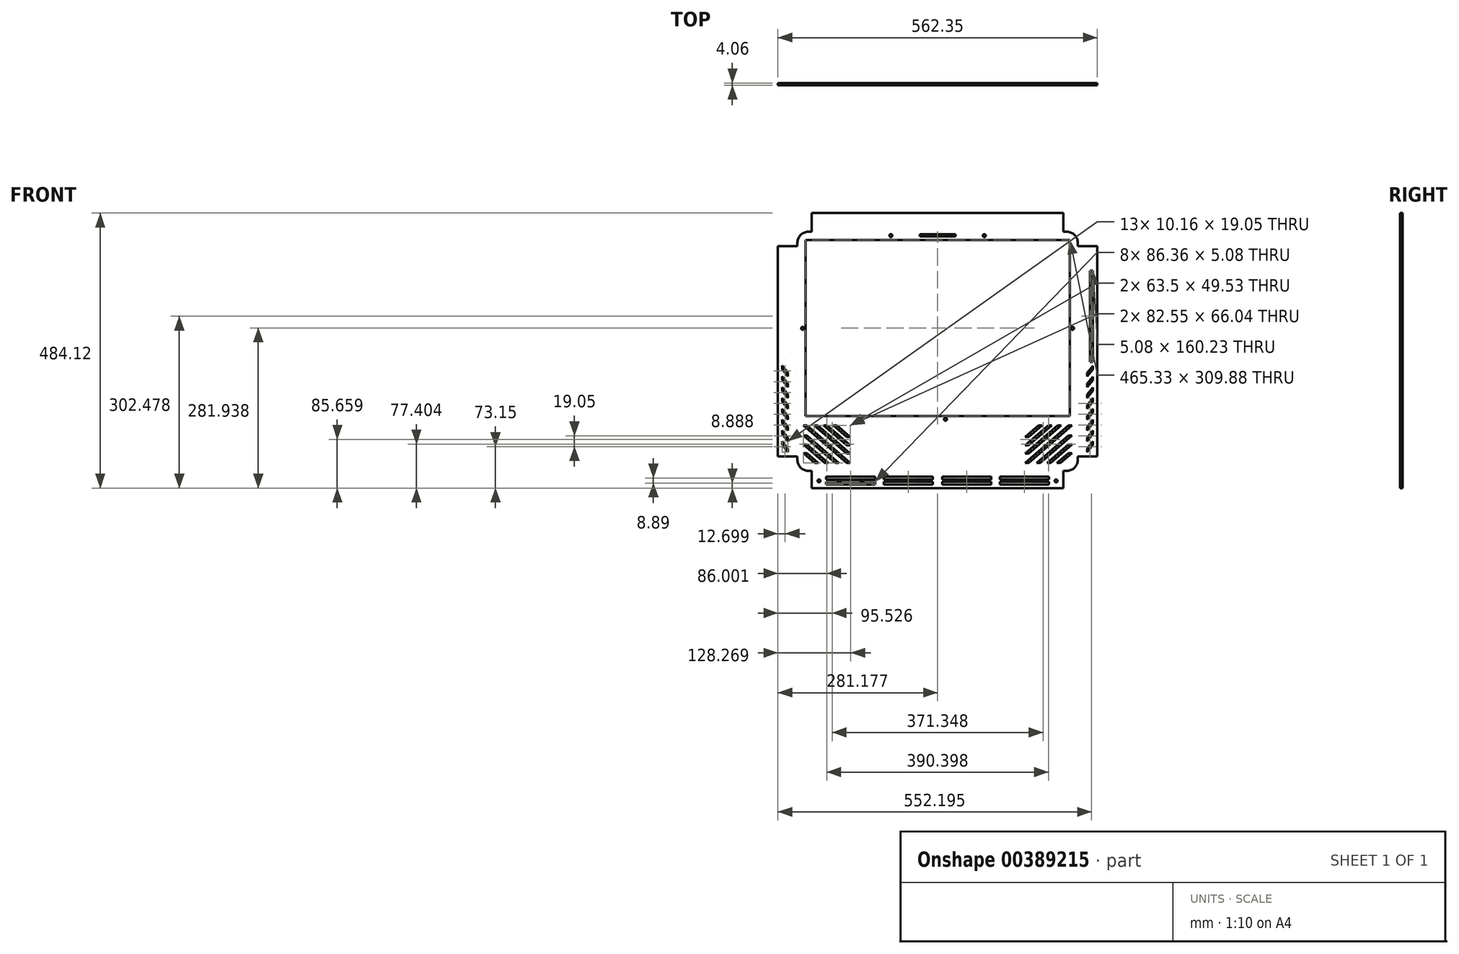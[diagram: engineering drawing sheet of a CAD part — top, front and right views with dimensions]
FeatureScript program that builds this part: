
annotation { "Feature Type Name" : "Feature", "Feature Type Description" : "" }
export const myFeature = defineFeature(function(context is Context, id is Id, definition is map)
    precondition{}
    {
        {
            var Q0;
            Q0=qCreatedBy(makeId("Front.planeOp"),FACE);
            var sketch = newSketch(context, id + "F0", { "sketchPlane" : qUnion([Q0])});
            skLineSegment(sketch, "E0.bottom", {"start": v(112.47, 222.87) * mm, "end": v(-343.2, 222.87) * mm});
            skLineSegment(sketch, "E0.top", {"start": v(112.47, -197.75) * mm, "end": v(-343.2, -197.75) * mm});
            skLineSegment(sketch, "E0.left", {"start": v(131.52, 203.82) * mm, "end": v(131.52, -178.7) * mm});
            skLineSegment(sketch, "E0.right", {"start": v(-362.25, 203.82) * mm, "end": v(-362.25, -178.7) * mm});
            skPoint(sketch, "E0.middle", {"position": v(-115.36, 12.56) * mm});
            skPoint(sketch, "E1.visualSharp", {"position": v(-362.25, 222.87) * mm});
            skArc(sketch, "E1.filletArc", {"start": v(-343.2, 222.87) * mm, "mid": v(-356.67, 217.3) * mm, "end": v(-362.25, 203.82) * mm});
            skPoint(sketch, "E2.visualSharp", {"position": v(131.52, 222.87) * mm});
            skArc(sketch, "E2.filletArc", {"start": v(131.52, 203.82) * mm, "mid": v(125.95, 217.3) * mm, "end": v(112.47, 222.87) * mm});
            skPoint(sketch, "E3.visualSharp", {"position": v(131.52, -197.75) * mm});
            skArc(sketch, "E3.filletArc", {"start": v(112.47, -197.75) * mm, "mid": v(125.95, -192.17) * mm, "end": v(131.52, -178.7) * mm});
            skPoint(sketch, "E4.visualSharp", {"position": v(-362.25, -197.75) * mm});
            skArc(sketch, "E4.filletArc", {"start": v(-362.25, -178.7) * mm, "mid": v(-356.67, -192.17) * mm, "end": v(-343.2, -197.75) * mm});
            skPoint(sketch, "E5.visualSharp", {"position": v(177.9, 212.68) * mm});
            skLineSegment(sketch, "E6.bottom", {"start": v(108.41, 218.8) * mm, "end": v(-339.14, 218.8) * mm});
            skLineSegment(sketch, "E6.left", {"start": v(127.46, 199.76) * mm, "end": v(127.46, -93.36) * mm});
            skLineSegment(sketch, "E6.right", {"start": v(-358.19, 199.76) * mm, "end": v(-358.19, -93.36) * mm});
            skPoint(sketch, "E7.visualSharp", {"position": v(127.46, 218.8) * mm});
            skArc(sketch, "E7.filletArc", {"start": v(127.46, 199.76) * mm, "mid": v(121.88, 213.23) * mm, "end": v(108.41, 218.8) * mm});
            skPoint(sketch, "E8.visualSharp", {"position": v(-358.19, 218.8) * mm});
            skArc(sketch, "E8.filletArc", {"start": v(-339.14, 218.8) * mm, "mid": v(-352.6, 213.23) * mm, "end": v(-358.19, 199.76) * mm});
            skPoint(sketch, "E9.visualSharp", {"position": v(-358.19, -112.4) * mm});
            skPoint(sketch, "E10.visualSharp", {"position": v(127.46, -112.4) * mm});
            skLineSegment(sketch, "E11.bottom", {"start": v(131.52, 197.47) * mm, "end": v(165.81, 197.47) * mm});
            skLineSegment(sketch, "E11.top", {"start": v(131.52, -172.35) * mm, "end": v(165.81, -172.35) * mm});
            skLineSegment(sketch, "E11.left", {"start": v(131.52, 197.47) * mm, "end": v(131.52, -172.35) * mm});
            skLineSegment(sketch, "E11.right", {"start": v(165.81, 197.47) * mm, "end": v(165.81, -172.35) * mm});
            skLineSegment(sketch, "E12.bottom", {"start": v(-396.54, 197.47) * mm, "end": v(-362.25, 197.47) * mm});
            skLineSegment(sketch, "E12.top", {"start": v(-396.54, -172.35) * mm, "end": v(-362.25, -172.35) * mm});
            skLineSegment(sketch, "E12.left", {"start": v(-396.54, 197.47) * mm, "end": v(-396.54, -172.35) * mm});
            skLineSegment(sketch, "E12.right", {"start": v(-362.25, 197.47) * mm, "end": v(-362.25, -172.35) * mm});
            skLineSegment(sketch, "E13.bottom", {"start": v(-336.85, 255.9) * mm, "end": v(106.12, 255.9) * mm});
            skLineSegment(sketch, "E13.top", {"start": v(-336.85, 222.87) * mm, "end": v(106.12, 222.87) * mm});
            skLineSegment(sketch, "E13.left", {"start": v(-336.85, 255.9) * mm, "end": v(-336.85, 222.87) * mm});
            skLineSegment(sketch, "E13.right", {"start": v(106.12, 255.9) * mm, "end": v(106.12, 222.87) * mm});
            skLineSegment(sketch, "E14.bottom", {"start": v(-336.85, -197.75) * mm, "end": v(106.12, -197.75) * mm});
            skLineSegment(sketch, "E14.top", {"start": v(-336.85, -228.23) * mm, "end": v(106.12, -228.23) * mm});
            skLineSegment(sketch, "E14.left", {"start": v(-336.85, -197.75) * mm, "end": v(-336.85, -228.23) * mm});
            skLineSegment(sketch, "E14.right", {"start": v(106.12, -197.75) * mm, "end": v(106.12, -228.23) * mm});
            skSolve(sketch);
        }
        {
            var Q0;
            Q0 = qSketchRegion(id + "F0", true);
            extrude(context, id + "F1", {"entities" : qUnion([Q0]), "depth" : 4.06 * mm});
        }
        {
            var Q0;
            Q0=qCreatedBy(makeId("Front.planeOp"),FACE);
            var sketch = newSketch(context, id + "F2", { "sketchPlane" : qUnion([Q0])});
            skPoint(sketch, "E15.visualSharp", {"position": v(-358.19, 218.8) * mm});
            skPoint(sketch, "E16.visualSharp", {"position": v(127.46, 218.8) * mm});
            skPoint(sketch, "E17.visualSharp", {"position": v(-358.19, -111.4) * mm});
            skPoint(sketch, "E18.visualSharp", {"position": v(127.46, -111.4) * mm});
            skLineSegment(sketch, "E19.bottom", {"start": v(-348.03, 208.65) * mm, "end": v(117.3, 208.65) * mm});
            skLineSegment(sketch, "E19.top", {"start": v(-348.03, -101.23) * mm, "end": v(117.3, -101.23) * mm});
            skLineSegment(sketch, "E19.left", {"start": v(-348.03, 208.65) * mm, "end": v(-348.03, -101.23) * mm});
            skLineSegment(sketch, "E19.right", {"start": v(117.3, 208.65) * mm, "end": v(117.3, -101.23) * mm});
            skSolve(sketch);
        }
        {
            var Q0;
            Q0 = qSketchRegion(id + "F2", true);
            extrude(context, id + "F3", {"entities" : qUnion([Q0]), "operationType" : NewBodyOperationType.REMOVE, "depth" : 4.06 * mm});
        }
        {
            var Q0;
            Q0=qCreatedBy(makeId("Front.planeOp"),FACE);
            var sketch = newSketch(context, id + "F4", { "sketchPlane" : qUnion([Q0])});
            skCircle(sketch, "E20", {"center": v(-101.4, -106.97) * mm, "radius": 2.54 * mm});
            skCircle(sketch, "E21", {"center": v(122.38, 53.05) * mm, "radius": 2.54 * mm});
            skCircle(sketch, "E22", {"center": v(-353.1, 53.05) * mm, "radius": 2.54 * mm});
            skCircle(sketch, "E23", {"center": v(-197.66, 216.27) * mm, "radius": 2.54 * mm});
            skCircle(sketch, "E24", {"center": v(-33.07, 216.27) * mm, "radius": 2.54 * mm});
            skLineSegment(sketch, "E25.bottom", {"start": v(-146.86, 218.8) * mm, "end": v(-83.87, 218.8) * mm});
            skLineSegment(sketch, "E25.top", {"start": v(-146.86, 215) * mm, "end": v(-83.87, 215) * mm});
            skLineSegment(sketch, "E25.left", {"start": v(-146.86, 218.8) * mm, "end": v(-146.86, 215) * mm});
            skLineSegment(sketch, "E25.right", {"start": v(-83.87, 218.8) * mm, "end": v(-83.87, 215) * mm});
            skSolve(sketch);
        }
        {
            var Q0;
            Q0 = qSketchRegion(id + "F4", true);
            extrude(context, id + "F5", {"entities" : qUnion([Q0]), "operationType" : NewBodyOperationType.REMOVE, "depth" : 25.4 * mm});
        }
        {
            var Q0;
            Q0=qCreatedBy(makeId("Front.planeOp"),FACE);
            var sketch = newSketch(context, id + "F6", { "sketchPlane" : qUnion([Q0])});
            skLineSegment(sketch, "E26", {"start": v(-351.81, -117.8) * mm, "end": v(-345.46, -117.8) * mm});
            skLineSegment(sketch, "E27", {"start": v(-345.46, -117.8) * mm, "end": v(-269.26, -183.85) * mm});
            skLineSegment(sketch, "E28", {"start": v(-269.26, -183.85) * mm, "end": v(-275.61, -183.85) * mm});
            skLineSegment(sketch, "E29", {"start": v(-275.61, -183.85) * mm, "end": v(-351.81, -117.8) * mm});
            skLineSegment(sketch, "E30", {"start": v(-332.76, -117.8) * mm, "end": v(-326.41, -117.8) * mm});
            skPoint(sketch, "E31.endSnap0", {"position": v(-272.44, -183.85) * mm});
            skLineSegment(sketch, "E32", {"start": v(-269.26, -167.34) * mm, "end": v(-275.61, -167.34) * mm});
            skLineSegment(sketch, "E33", {"start": v(-275.61, -167.34) * mm, "end": v(-332.76, -117.8) * mm});
            skLineSegment(sketch, "E34", {"start": v(-326.41, -117.8) * mm, "end": v(-269.26, -167.34) * mm});
            skLineSegment(sketch, "E35", {"start": v(-351.81, -135.42) * mm, "end": v(-345.46, -135.42) * mm});
            skLineSegment(sketch, "E36", {"start": v(-345.46, -135.42) * mm, "end": v(-289.6, -183.85) * mm});
            skLineSegment(sketch, "E37", {"start": v(-289.6, -183.85) * mm, "end": v(-295.94, -183.85) * mm});
            skLineSegment(sketch, "E38", {"start": v(-295.94, -183.85) * mm, "end": v(-351.81, -135.42) * mm});
            skLineSegment(sketch, "E39", {"start": v(-351.81, -151.37) * mm, "end": v(-345.46, -151.37) * mm});
            skLineSegment(sketch, "E40", {"start": v(-345.46, -151.37) * mm, "end": v(-307.99, -183.85) * mm});
            skLineSegment(sketch, "E41", {"start": v(-307.99, -183.85) * mm, "end": v(-314.34, -183.85) * mm});
            skLineSegment(sketch, "E42", {"start": v(-314.34, -183.85) * mm, "end": v(-351.81, -151.37) * mm});
            skLineSegment(sketch, "E43", {"start": v(-351.81, -166.54) * mm, "end": v(-345.46, -166.54) * mm});
            skLineSegment(sketch, "E44", {"start": v(-345.46, -166.54) * mm, "end": v(-325.5, -183.85) * mm});
            skLineSegment(sketch, "E45", {"start": v(-325.5, -183.85) * mm, "end": v(-331.85, -183.85) * mm});
            skLineSegment(sketch, "E46", {"start": v(-331.85, -183.85) * mm, "end": v(-351.81, -166.54) * mm});
            skLineSegment(sketch, "E47", {"start": v(-269.26, -153.13) * mm, "end": v(-275.61, -153.13) * mm});
            skLineSegment(sketch, "E48", {"start": v(-275.61, -153.13) * mm, "end": v(-316.37, -117.8) * mm});
            skLineSegment(sketch, "E49", {"start": v(-316.37, -117.8) * mm, "end": v(-310.02, -117.8) * mm});
            skLineSegment(sketch, "E50", {"start": v(-310.02, -117.8) * mm, "end": v(-269.26, -153.13) * mm});
            skLineSegment(sketch, "E51", {"start": v(-269.26, -138.28) * mm, "end": v(-275.61, -138.28) * mm});
            skLineSegment(sketch, "E52", {"start": v(-275.61, -138.28) * mm, "end": v(-299.24, -117.8) * mm});
            skLineSegment(sketch, "E53", {"start": v(-299.24, -117.8) * mm, "end": v(-292.89, -117.8) * mm});
            skLineSegment(sketch, "E54", {"start": v(-292.89, -117.8) * mm, "end": v(-269.26, -138.28) * mm});
            skLineSegment(sketch, "E55.MirrorCS", {"start": v(102.08, -117.8) * mm, "end": v(95.73, -117.8) * mm});
            skLineSegment(sketch, "E56.MirrorCS", {"start": v(121.13, -117.8) * mm, "end": v(114.78, -117.8) * mm});
            skLineSegment(sketch, "E57.MirrorCS", {"start": v(85.7, -117.8) * mm, "end": v(79.34, -117.8) * mm});
            skLineSegment(sketch, "E58.MirrorCS", {"start": v(38.58, -138.28) * mm, "end": v(44.93, -138.28) * mm});
            skLineSegment(sketch, "E59.MirrorCS", {"start": v(68.56, -117.8) * mm, "end": v(62.2, -117.8) * mm});
            skLineSegment(sketch, "E60.MirrorCS", {"start": v(121.13, -151.37) * mm, "end": v(114.78, -151.37) * mm});
            skLineSegment(sketch, "E61.MirrorCS", {"start": v(58.91, -183.85) * mm, "end": v(65.26, -183.85) * mm});
            skLineSegment(sketch, "E62.MirrorCS", {"start": v(38.58, -167.34) * mm, "end": v(44.93, -167.34) * mm});
            skLineSegment(sketch, "E63.MirrorCS", {"start": v(38.58, -183.85) * mm, "end": v(44.93, -183.85) * mm});
            skLineSegment(sketch, "E64.MirrorCS", {"start": v(94.82, -183.85) * mm, "end": v(101.17, -183.85) * mm});
            skLineSegment(sketch, "E65.MirrorCS", {"start": v(38.58, -153.13) * mm, "end": v(44.93, -153.13) * mm});
            skLineSegment(sketch, "E66.MirrorCS", {"start": v(121.13, -166.54) * mm, "end": v(114.78, -166.54) * mm});
            skLineSegment(sketch, "E67.MirrorCS", {"start": v(121.13, -135.42) * mm, "end": v(114.78, -135.42) * mm});
            skLineSegment(sketch, "E68.MirrorCS", {"start": v(77.3, -183.85) * mm, "end": v(83.66, -183.85) * mm});
            skLineSegment(sketch, "E69.MirrorCS", {"start": v(114.78, -166.54) * mm, "end": v(94.82, -183.85) * mm});
            skLineSegment(sketch, "E70.MirrorCS", {"start": v(44.93, -183.85) * mm, "end": v(121.13, -117.8) * mm});
            skLineSegment(sketch, "E71.MirrorCS", {"start": v(79.34, -117.8) * mm, "end": v(38.58, -153.13) * mm});
            skLineSegment(sketch, "E72.MirrorCS", {"start": v(114.78, -117.8) * mm, "end": v(38.58, -183.85) * mm});
            skLineSegment(sketch, "E73.MirrorCS", {"start": v(83.66, -183.85) * mm, "end": v(121.13, -151.37) * mm});
            skLineSegment(sketch, "E74.MirrorCS", {"start": v(114.78, -151.37) * mm, "end": v(77.3, -183.85) * mm});
            skLineSegment(sketch, "E75.MirrorCS", {"start": v(44.93, -138.28) * mm, "end": v(68.56, -117.8) * mm});
            skLineSegment(sketch, "E76.MirrorCS", {"start": v(101.17, -183.85) * mm, "end": v(121.13, -166.54) * mm});
            skLineSegment(sketch, "E77.MirrorCS", {"start": v(44.93, -167.34) * mm, "end": v(102.08, -117.8) * mm});
            skLineSegment(sketch, "E78.MirrorCS", {"start": v(62.2, -117.8) * mm, "end": v(38.58, -138.28) * mm});
            skPoint(sketch, "E79.MirrorP", {"position": v(41.76, -183.85) * mm});
            skLineSegment(sketch, "E80.MirrorCS", {"start": v(65.26, -183.85) * mm, "end": v(121.13, -135.42) * mm});
            skLineSegment(sketch, "E81.MirrorCS", {"start": v(44.93, -153.13) * mm, "end": v(85.7, -117.8) * mm});
            skLineSegment(sketch, "E82.MirrorCS", {"start": v(114.78, -135.42) * mm, "end": v(58.91, -183.85) * mm});
            skLineSegment(sketch, "E83.MirrorCS", {"start": v(95.73, -117.8) * mm, "end": v(38.58, -167.34) * mm});
            skSolve(sketch);
        }
        {
            var Q0;
            Q0 = qSketchRegion(id + "F6", true);
            extrude(context, id + "F7", {"entities" : qUnion([Q0]), "operationType" : NewBodyOperationType.REMOVE, "depth" : 25.4 * mm});
        }
        {
            var Q0;
            Q0=qCreatedBy(makeId("Front.planeOp"),FACE);
            var sketch = newSketch(context, id + "F8", { "sketchPlane" : qUnion([Q0])});
            skLineSegment(sketch, "E84", {"start": v(158.2, -12.86) * mm, "end": v(158.2, -19.21) * mm});
            skLineSegment(sketch, "E85", {"start": v(158.2, -31.91) * mm, "end": v(158.2, -38.26) * mm});
            skLineSegment(sketch, "E86", {"start": v(148.03, -24.92) * mm, "end": v(148.03, -31.26) * mm});
            skLineSegment(sketch, "E87", {"start": v(148.03, -31.26) * mm, "end": v(158.2, -19.21) * mm});
            skLineSegment(sketch, "E88", {"start": v(158.2, -12.86) * mm, "end": v(148.03, -24.92) * mm});
            skLineSegment(sketch, "E89", {"start": v(148.03, -43.96) * mm, "end": v(148.03, -50.3) * mm});
            skLineSegment(sketch, "E90", {"start": v(148.03, -43.96) * mm, "end": v(158.2, -31.91) * mm});
            skLineSegment(sketch, "E91", {"start": v(158.2, -38.26) * mm, "end": v(148.03, -50.3) * mm});
            skLineSegment(sketch, "E92", {"start": v(148.03, -63) * mm, "end": v(148.03, -69.36) * mm});
            skLineSegment(sketch, "E93", {"start": v(158.2, -50.96) * mm, "end": v(158.2, -56.66) * mm});
            skLineSegment(sketch, "E94", {"start": v(148.03, -63) * mm, "end": v(158.2, -50.96) * mm});
            skLineSegment(sketch, "E95", {"start": v(158.2, -56.66) * mm, "end": v(148.03, -69.36) * mm});
            skLineSegment(sketch, "E96", {"start": v(148.03, -82.06) * mm, "end": v(148.03, -88.41) * mm});
            skLineSegment(sketch, "E97", {"start": v(158.2, -75.71) * mm, "end": v(158.2, -69.36) * mm});
            skLineSegment(sketch, "E98", {"start": v(148.03, -82.06) * mm, "end": v(158.2, -69.36) * mm});
            skLineSegment(sketch, "E99", {"start": v(158.2, -75.71) * mm, "end": v(148.03, -88.41) * mm});
            skLineSegment(sketch, "E100", {"start": v(148.03, -101.11) * mm, "end": v(148.03, -107.46) * mm});
            skLineSegment(sketch, "E101", {"start": v(148.03, -107.46) * mm, "end": v(158.2, -94.76) * mm});
            skLineSegment(sketch, "E102", {"start": v(158.2, -94.76) * mm, "end": v(158.2, -88.41) * mm});
            skLineSegment(sketch, "E103", {"start": v(158.2, -88.41) * mm, "end": v(148.03, -101.11) * mm});
            skLineSegment(sketch, "E104", {"start": v(148.03, -120.16) * mm, "end": v(148.03, -126.51) * mm});
            skLineSegment(sketch, "E105", {"start": v(148.03, -126.51) * mm, "end": v(158.2, -113.81) * mm});
            skLineSegment(sketch, "E106", {"start": v(158.2, -113.81) * mm, "end": v(158.2, -107.46) * mm});
            skLineSegment(sketch, "E107", {"start": v(158.2, -107.46) * mm, "end": v(148.03, -120.16) * mm});
            skLineSegment(sketch, "E108", {"start": v(148.03, -139.21) * mm, "end": v(148.03, -145.56) * mm});
            skLineSegment(sketch, "E109", {"start": v(148.03, -145.56) * mm, "end": v(158.2, -132.86) * mm});
            skLineSegment(sketch, "E110", {"start": v(158.2, -132.86) * mm, "end": v(158.2, -126.51) * mm});
            skLineSegment(sketch, "E111", {"start": v(158.2, -126.51) * mm, "end": v(148.03, -139.21) * mm});
            skLineSegment(sketch, "E112", {"start": v(148.03, -158.26) * mm, "end": v(148.03, -164.61) * mm});
            skLineSegment(sketch, "E113", {"start": v(148.03, -164.61) * mm, "end": v(158.2, -151.91) * mm});
            skLineSegment(sketch, "E114", {"start": v(158.2, -151.91) * mm, "end": v(158.2, -145.56) * mm});
            skLineSegment(sketch, "E115", {"start": v(158.2, -145.56) * mm, "end": v(148.03, -158.26) * mm});
            skLineSegment(sketch, "E116", {"start": v(-388.92, -145.56) * mm, "end": v(-388.92, -151.9) * mm});
            skLineSegment(sketch, "E117", {"start": v(-388.92, -151.9) * mm, "end": v(-378.76, -164.6) * mm});
            skLineSegment(sketch, "E118", {"start": v(-378.76, -164.6) * mm, "end": v(-378.76, -158.26) * mm});
            skLineSegment(sketch, "E119", {"start": v(-378.76, -158.26) * mm, "end": v(-388.92, -145.56) * mm});
            skLineSegment(sketch, "E120", {"start": v(-388.92, -132.86) * mm, "end": v(-388.92, -126.5) * mm});
            skLineSegment(sketch, "E121", {"start": v(-388.92, -126.5) * mm, "end": v(-378.76, -139.2) * mm});
            skLineSegment(sketch, "E122", {"start": v(-378.76, -139.2) * mm, "end": v(-378.76, -145.56) * mm});
            skLineSegment(sketch, "E123", {"start": v(-378.76, -145.56) * mm, "end": v(-388.92, -132.86) * mm});
            skLineSegment(sketch, "E124", {"start": v(-378.76, -126.5) * mm, "end": v(-378.76, -120.16) * mm});
            skLineSegment(sketch, "E125", {"start": v(-378.76, -120.16) * mm, "end": v(-388.92, -107.46) * mm});
            skLineSegment(sketch, "E126", {"start": v(-388.92, -107.46) * mm, "end": v(-388.92, -113.8) * mm});
            skLineSegment(sketch, "E127", {"start": v(-388.92, -113.8) * mm, "end": v(-378.76, -126.5) * mm});
            skLineSegment(sketch, "E128", {"start": v(-378.76, -107.46) * mm, "end": v(-388.92, -94.76) * mm});
            skLineSegment(sketch, "E129", {"start": v(-388.92, -94.76) * mm, "end": v(-388.92, -88.4) * mm});
            skLineSegment(sketch, "E130", {"start": v(-388.92, -88.4) * mm, "end": v(-378.76, -101.1) * mm});
            skLineSegment(sketch, "E131", {"start": v(-378.76, -101.1) * mm, "end": v(-378.76, -107.46) * mm});
            skLineSegment(sketch, "E132", {"start": v(-378.76, -88.4) * mm, "end": v(-388.92, -75.7) * mm});
            skLineSegment(sketch, "E133", {"start": v(-388.92, -75.7) * mm, "end": v(-388.92, -69.36) * mm});
            skLineSegment(sketch, "E134", {"start": v(-388.92, -69.36) * mm, "end": v(-378.76, -82.06) * mm});
            skLineSegment(sketch, "E135", {"start": v(-378.76, -82.06) * mm, "end": v(-378.76, -88.4) * mm});
            skLineSegment(sketch, "E136", {"start": v(-378.76, -69.36) * mm, "end": v(-388.92, -56.66) * mm});
            skLineSegment(sketch, "E137", {"start": v(-388.92, -56.66) * mm, "end": v(-388.92, -50.3) * mm});
            skLineSegment(sketch, "E138", {"start": v(-388.92, -50.3) * mm, "end": v(-378.76, -63) * mm});
            skLineSegment(sketch, "E139", {"start": v(-378.76, -63) * mm, "end": v(-378.76, -69.36) * mm});
            skLineSegment(sketch, "E140", {"start": v(-378.76, -50.3) * mm, "end": v(-388.92, -37.6) * mm});
            skLineSegment(sketch, "E141", {"start": v(-388.92, -37.6) * mm, "end": v(-388.92, -31.26) * mm});
            skLineSegment(sketch, "E142", {"start": v(-388.92, -31.26) * mm, "end": v(-378.76, -43.96) * mm});
            skLineSegment(sketch, "E143", {"start": v(-378.76, -43.96) * mm, "end": v(-378.76, -50.3) * mm});
            skLineSegment(sketch, "E144", {"start": v(-378.76, -31.26) * mm, "end": v(-388.92, -18.56) * mm});
            skLineSegment(sketch, "E145", {"start": v(-388.92, -18.56) * mm, "end": v(-388.92, -12.2) * mm});
            skLineSegment(sketch, "E146", {"start": v(-388.92, -12.2) * mm, "end": v(-378.76, -24.9) * mm});
            skLineSegment(sketch, "E147", {"start": v(-378.76, -24.9) * mm, "end": v(-378.76, -31.26) * mm});
            skLineSegment(sketch, "E148.bottom", {"start": v(153.11, -5.87) * mm, "end": v(158.2, -5.87) * mm});
            skLineSegment(sketch, "E148.top", {"start": v(153.11, 154.37) * mm, "end": v(158.2, 154.37) * mm});
            skLineSegment(sketch, "E148.left", {"start": v(153.11, -5.87) * mm, "end": v(153.11, 154.37) * mm});
            skLineSegment(sketch, "E148.right", {"start": v(158.2, -5.87) * mm, "end": v(158.2, 154.37) * mm});
            skLineSegment(sketch, "E149", {"start": v(-311.45, -221.88) * mm, "end": v(-225.1, -221.88) * mm});
            skLineSegment(sketch, "E150", {"start": v(-225.1, -221.88) * mm, "end": v(-225.1, -216.8) * mm});
            skLineSegment(sketch, "E151", {"start": v(-225.1, -216.8) * mm, "end": v(-311.45, -216.8) * mm});
            skLineSegment(sketch, "E152", {"start": v(-311.45, -216.8) * mm, "end": v(-311.45, -221.88) * mm});
            skLineSegment(sketch, "E153", {"start": v(-311.45, -213) * mm, "end": v(-311.45, -207.91) * mm});
            skLineSegment(sketch, "E154", {"start": v(-311.45, -207.91) * mm, "end": v(-225.1, -207.91) * mm});
            skLineSegment(sketch, "E155", {"start": v(-225.1, -207.91) * mm, "end": v(-225.1, -213) * mm});
            skLineSegment(sketch, "E156", {"start": v(-225.1, -213) * mm, "end": v(-311.45, -213) * mm});
            skLineSegment(sketch, "E157", {"start": v(-209.85, -207.91) * mm, "end": v(-209.85, -213) * mm});
            skLineSegment(sketch, "E158", {"start": v(-209.85, -213) * mm, "end": v(-123.5, -213) * mm});
            skLineSegment(sketch, "E159", {"start": v(-123.5, -213) * mm, "end": v(-123.5, -207.91) * mm});
            skLineSegment(sketch, "E160", {"start": v(-123.5, -207.91) * mm, "end": v(-209.85, -207.91) * mm});
            skLineSegment(sketch, "E161", {"start": v(-209.85, -216.8) * mm, "end": v(-209.85, -221.88) * mm});
            skLineSegment(sketch, "E162", {"start": v(-209.85, -221.88) * mm, "end": v(-123.5, -221.88) * mm});
            skLineSegment(sketch, "E163", {"start": v(-123.5, -221.88) * mm, "end": v(-123.5, -216.8) * mm});
            skLineSegment(sketch, "E164", {"start": v(-123.5, -216.8) * mm, "end": v(-209.85, -216.8) * mm});
            skLineSegment(sketch, "E165", {"start": v(-107.24, -207.91) * mm, "end": v(-107.24, -213) * mm});
            skLineSegment(sketch, "E166", {"start": v(-107.24, -213) * mm, "end": v(-20.88, -213) * mm});
            skLineSegment(sketch, "E167", {"start": v(-20.88, -213) * mm, "end": v(-20.88, -207.91) * mm});
            skLineSegment(sketch, "E168", {"start": v(-20.88, -207.91) * mm, "end": v(-107.24, -207.91) * mm});
            skLineSegment(sketch, "E169", {"start": v(-107.24, -216.8) * mm, "end": v(-107.24, -221.88) * mm});
            skLineSegment(sketch, "E170", {"start": v(-107.24, -221.88) * mm, "end": v(-20.88, -221.88) * mm});
            skLineSegment(sketch, "E171", {"start": v(-20.88, -221.88) * mm, "end": v(-20.88, -216.8) * mm});
            skLineSegment(sketch, "E172", {"start": v(-20.88, -216.8) * mm, "end": v(-107.24, -216.8) * mm});
            skLineSegment(sketch, "E173", {"start": v(-5.64, -213) * mm, "end": v(-5.64, -207.91) * mm});
            skLineSegment(sketch, "E174", {"start": v(-5.64, -207.91) * mm, "end": v(80.72, -207.91) * mm});
            skLineSegment(sketch, "E175", {"start": v(80.72, -207.91) * mm, "end": v(80.72, -213) * mm});
            skLineSegment(sketch, "E176", {"start": v(80.72, -213) * mm, "end": v(-5.64, -213) * mm});
            skLineSegment(sketch, "E177", {"start": v(-5.64, -216.8) * mm, "end": v(-5.64, -221.88) * mm});
            skLineSegment(sketch, "E178", {"start": v(-5.64, -221.88) * mm, "end": v(80.72, -221.88) * mm});
            skLineSegment(sketch, "E179", {"start": v(80.72, -221.88) * mm, "end": v(80.72, -216.8) * mm});
            skLineSegment(sketch, "E180", {"start": v(80.72, -216.8) * mm, "end": v(-5.64, -216.8) * mm});
            skCircle(sketch, "E181", {"center": v(93.42, -215.53) * mm, "radius": 2.5 * mm});
            skCircle(sketch, "E182", {"center": v(-324.15, -215.53) * mm, "radius": 2.5 * mm});
            skSolve(sketch);
        }
        {
            var Q0;
            Q0 = qSketchRegion(id + "F8", true);
            extrude(context, id + "F9", {"entities" : qUnion([Q0]), "operationType" : NewBodyOperationType.REMOVE, "depth" : 25.4 * mm});
        }
    });
